# Revit family: equip-water-cooler-hlsy-tylr-oval2-bi-level-reverse
name_source: partatom
category: Plumbing Fixtures
units: mm (PartAtom-declared; Revit-internal decimal feet)

## family parameters
Always vertical = Yes
Cut with Voids When Loaded = No
OmniClass Number = 23.45.00.00
OmniClass Title = Sanitary, Laundry, and Cleaning Equipment
Part Type = Normal
Room Calculation Point = No
Round Connector Dimension = Use Radius
Shared = No
Work Plane-Based = No

## types (3) — shared parameters
Apparent Load Phase 1 = 0 VA
Bubbler = Double Bubbler
CW Connection = Yes
Chiller Option = No
Cooler Depth = 1' - 6"
Cooler Width = 3' - 2 1/2"
Description = Water Cooler
HW Connection = No
Left Hand Unit = No
Lower Unit Rim Height = 2' - 10"
Manufacturer = Halsey Taylor
Mounting = 731593951550
Number of Poles = 1
Right Hand Unit = No
Sanitary Service Size Radius = 0' - 0 5/8"
URL = http://www.halseytaylor.com
Upper Unit Rim Height = 3' - 4"
Vent Connection = No
Version = 1.0.0.0
Voltage = 0 V
Volts/Hertz = 115V/60Hz
Waste Connection = Yes
Water Service Flow = 0 GPM
Water Service Flow Out = 0 GPM
Water Service Size Radius = 0' - 0 1/4"
zero-valued in all types: Power Factor

## per-type parameters (varying)
| type | Basin Material | Body Material | Bubbler Material | Model | Panel Material | Wall Plate Material |
| OVL-II ESR-Q BLK BASIN | Metal - Steel - Stainless - Onyx Black | Metal - Steel - Stainless - Chrome | Metal - Steel - Stainless - Chrome | OVL-II ESR-Q  BLK BASIN | Metal - Steel - Stainless - Chrome | Metal - Steel - Stainless - Chrome |
| OVL-II ESR-1-AG | Metal - Steel - Stainless - Aztec Gold | Metal - Steel - Stainless - Aztec Gold | Metal - Steel - Stainless - Aztec Gold | OVL-II ESR-1-AG | Metal - Steel - Stainless - Aztec Gold | Metal - Steel - Stainless - Aztec Gold |
| OVL-II ESR-Q | Metal - Steel - Stainless - Chrome | Metal - Steel - Stainless - Chrome | Metal - Steel - Stainless - Chrome | OVL-II ESR-Q | Metal - Steel - Stainless - Chrome | Metal - Steel - Stainless - Chrome |

## geometry (parser evidence)
native form markers: Sweep x6
no freeform markers — native parametric forms only
